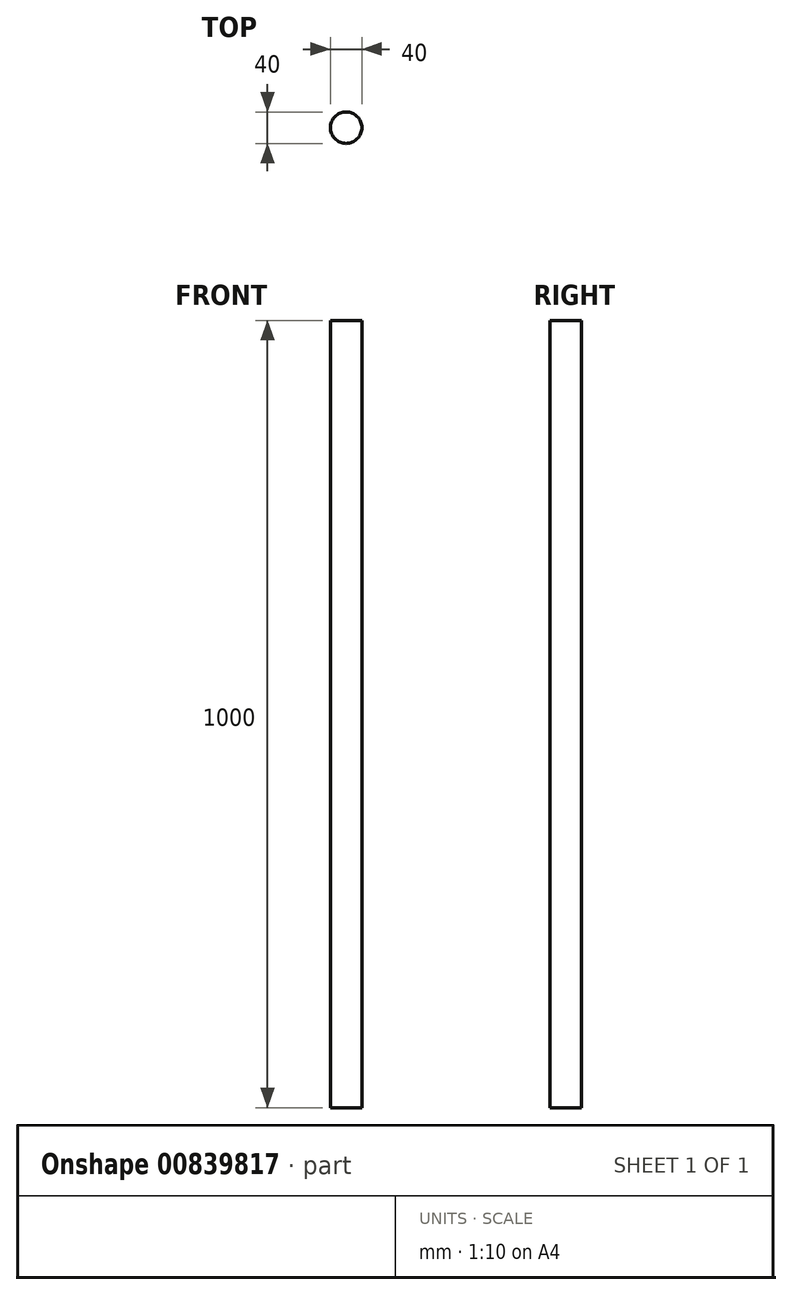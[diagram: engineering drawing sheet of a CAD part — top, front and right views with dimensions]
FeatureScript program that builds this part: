
annotation { "Feature Type Name" : "Feature", "Feature Type Description" : "" }
export const myFeature = defineFeature(function(context is Context, id is Id, definition is map)
    precondition{}
    {
        {
            var Q0;
            Q0=qCreatedBy(makeId("Top.planeOp"),FACE);
            var sketch = newSketch(context, id + "F0", { "sketchPlane" : qUnion([Q0])});
            skCircle(sketch, "E0", {"center": v(0, 0) * mm, "radius": 20 * mm});
            skSolve(sketch);
        }
        {
            var Q0;
            Q0=makeQuery(id+"F0.imprint","IMPRINT",FACE,{"disambiguationData":[TD([[makeQuery(id+"F0.imprint","IMPRINT",EDGE,{"derivedFrom":sQuery(id+"F0.wireOp",EDGE,"E0")}),1.0]])]});
            extrude(context, id + "F1", {"entities" : qUnion([Q0]), "depth" : 1000 * mm, "offsetDistance" : 25 * mm});
        }
    });
